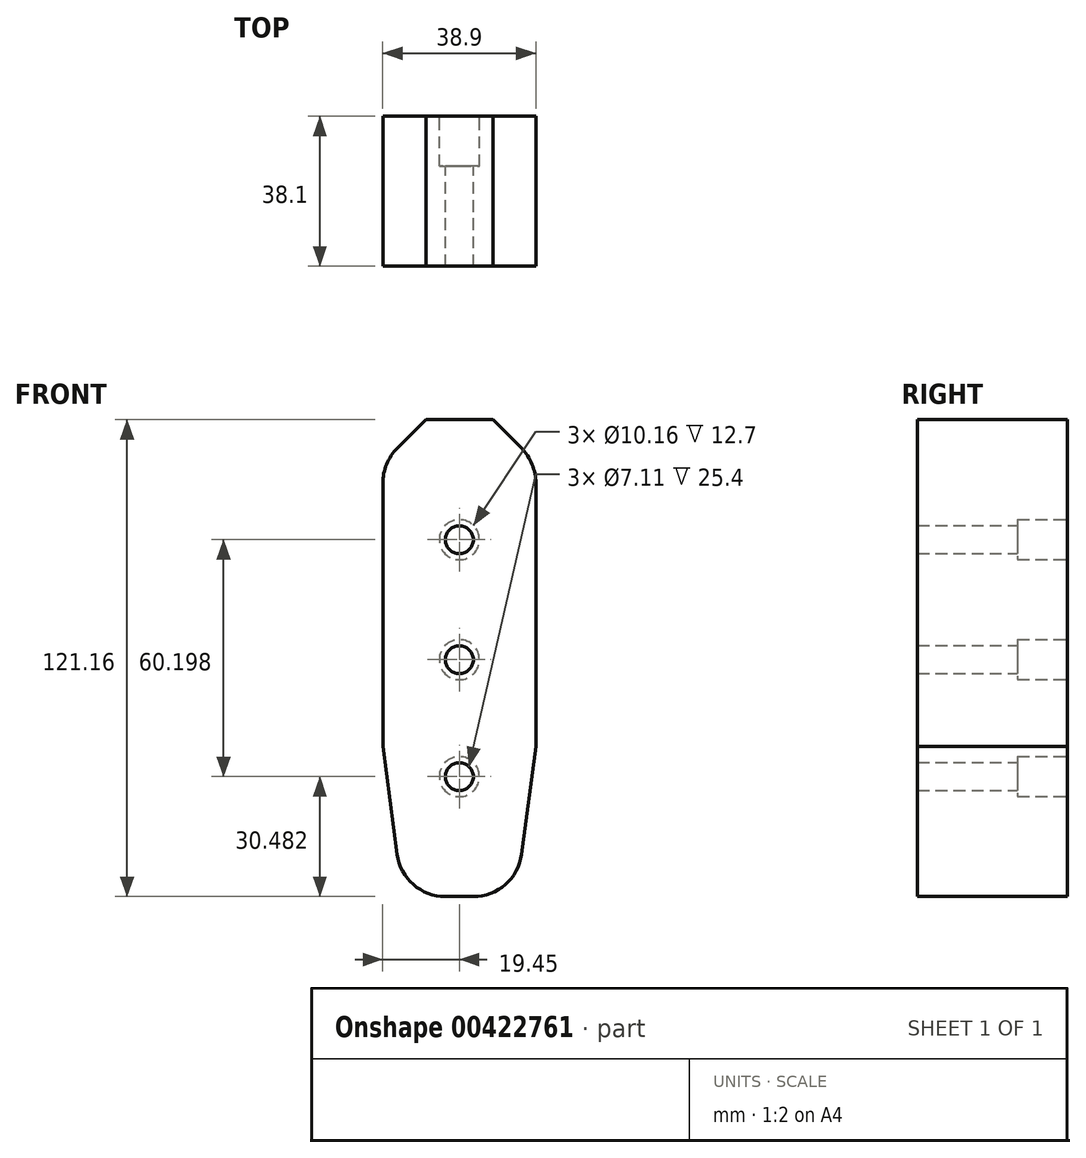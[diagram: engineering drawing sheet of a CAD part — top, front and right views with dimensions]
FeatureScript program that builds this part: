
annotation { "Feature Type Name" : "Feature", "Feature Type Description" : "" }
export const myFeature = defineFeature(function(context is Context, id is Id, definition is map)
    precondition{}
    {
        {
            var Q0;
            Q0=qCreatedBy(makeId("Front.planeOp"),FACE);
            var sketch = newSketch(context, id + "F0", { "sketchPlane" : qUnion([Q0])});
            skLineSegment(sketch, "E0", {"start": v(19.45, 50.8) * mm, "end": v(-19.45, 50.8) * mm});
            skLineSegment(sketch, "E1", {"start": v(19.45, 50.8) * mm, "end": v(19.45, -70.36) * mm});
            skLineSegment(sketch, "E2", {"start": v(-19.45, 50.8) * mm, "end": v(-19.45, -70.36) * mm});
            skLineSegment(sketch, "E3", {"start": v(19.45, -70.36) * mm, "end": v(-19.45, -70.36) * mm});
            skSolve(sketch);
        }
        {
            var Q0;
            Q0 = qSketchRegion(id + "F0", true);
            extrude(context, id + "F1", {"entities" : qUnion([Q0]), "oppositeDirection" : true, "depth" : 38.1 * mm, "offsetDistance" : 25.4 * mm});
        }
        {
            var Q0;
            Q0=makeQuery(id+"F1.opExtrude","SWEPT_EDGE",EDGE,{"disambiguationData":[OSD([sQuery(id+"F0.wireOp",EDGE,"5a9edbc7-dbc8-452a-a94e-e9a3c7398107"),sQuery(id+"F0.wireOp",EDGE,"E0")])]});
            var Q1;
            Q1=makeQuery(id+"F1.opExtrude","SWEPT_EDGE",EDGE,{"disambiguationData":[OSD([sQuery(id+"F0.wireOp",EDGE,"E0"),sQuery(id+"F0.wireOp",EDGE,"e4f6d671-606f-493e-a44e-61b159010204")])]});
            chamfer(context, id + "F2", {"entities" : qUnion([Q0, Q1]), "width" : 10.92 * mm, "tangentPropagation" : true});
        }
        {
            var Q0;
            {var subQ0=sQuery(id+"F0.wireOp",EDGE,"E1");Q0=makeQuery(id+"F2.opChamfer","BLEND_EDGE",EDGE,{"blendedFrom":[makeQuery(id+"F1.opExtrude","SWEPT_EDGE",EDGE,{"disambiguationData":[OSD([sQuery(id+"F0.wireOp",EDGE,"E0"),subQ0])]}),makeQuery(id+"F1.opExtrude","SWEPT_FACE",FACE,{"disambiguationData":[OSD([subQ0])]})],"blendedInto":[makeQuery(id+"F1.opExtrude","SWEPT_FACE",FACE,{"disambiguationData":[OSD([subQ0])]})]});}
            var Q1;
            {var subQ0=sQuery(id+"F0.wireOp",EDGE,"E2");Q1=makeQuery(id+"F2.opChamfer","BLEND_EDGE",EDGE,{"blendedFrom":[makeQuery(id+"F1.opExtrude","SWEPT_EDGE",EDGE,{"disambiguationData":[OSD([sQuery(id+"F0.wireOp",EDGE,"E0"),subQ0])]}),makeQuery(id+"F1.opExtrude","SWEPT_FACE",FACE,{"disambiguationData":[OSD([subQ0])]})],"blendedInto":[makeQuery(id+"F1.opExtrude","SWEPT_FACE",FACE,{"disambiguationData":[OSD([subQ0])]})]});}
            fillet(context, id + "F3", {"entities" : qUnion([Q0, Q1]), "radius" : 12.7 * mm, "tangentPropagation" : true, "allowEdgeOverflow" : false});
        }
        {
            var Q0;
            Q0=makeQuery(id+"F1.opExtrude","SWEPT_EDGE",EDGE,{"disambiguationData":[OSD([sQuery(id+"F0.wireOp",EDGE,"E2"),sQuery(id+"F0.wireOp",EDGE,"E3")])]});
            var Q1;
            Q1=makeQuery(id+"F1.opExtrude","SWEPT_EDGE",EDGE,{"disambiguationData":[OSD([sQuery(id+"F0.wireOp",EDGE,"E1"),sQuery(id+"F0.wireOp",EDGE,"E3")])]});
            chamfer(context, id + "F4", {"entities" : qUnion([Q0, Q1]), "chamferType" : ChamferType.TWO_OFFSETS, "width1" : 38.1 * mm, "oppositeDirection" : false, "width2" : 5.08 * mm, "tangentPropagation" : true});
        }
        {
            var Q0;
            {var subQ0=sQuery(id+"F0.wireOp",EDGE,"E3");Q0=makeQuery(id+"F4.opChamfer","BLEND_EDGE",EDGE,{"blendedFrom":[makeQuery(id+"F1.opExtrude","SWEPT_EDGE",EDGE,{"disambiguationData":[OSD([sQuery(id+"F0.wireOp",EDGE,"E1"),subQ0])]}),makeQuery(id+"F1.opExtrude","SWEPT_FACE",FACE,{"disambiguationData":[OSD([subQ0])]})],"blendedInto":[makeQuery(id+"F1.opExtrude","SWEPT_FACE",FACE,{"disambiguationData":[OSD([subQ0])]})]});}
            var Q1;
            {var subQ0=sQuery(id+"F0.wireOp",EDGE,"E3");Q1=makeQuery(id+"F4.opChamfer","BLEND_EDGE",EDGE,{"blendedFrom":[makeQuery(id+"F1.opExtrude","SWEPT_EDGE",EDGE,{"disambiguationData":[OSD([sQuery(id+"F0.wireOp",EDGE,"E2"),subQ0])]}),makeQuery(id+"F1.opExtrude","SWEPT_FACE",FACE,{"disambiguationData":[OSD([subQ0])]})],"blendedInto":[makeQuery(id+"F1.opExtrude","SWEPT_FACE",FACE,{"disambiguationData":[OSD([subQ0])]})]});}
            fillet(context, id + "F5", {"entities" : qUnion([Q0, Q1]), "radius" : 12.38 * mm, "tangentPropagation" : true, "allowEdgeOverflow" : false});
        }
        {
            var Q0;
            Q0=makeQuery(id+"F1.opExtrude","CAP_FACE",FACE,{"disambiguationData":[OSD([sQuery(id+"F0.wireOp",EDGE,"E0"),sQuery(id+"F0.wireOp",EDGE,"E1"),sQuery(id+"F0.wireOp",EDGE,"E2"),sQuery(id+"F0.wireOp",EDGE,"E3")])],"isStart":false});
            var sketch = newSketch(context, id + "F6", { "sketchPlane" : qUnion([Q0])});
            skCircle(sketch, "E4", {"center": v(0, -39.88) * mm, "radius": 5.08 * mm});
            skCircle(sketch, "E5", {"center": v(0, -10.16) * mm, "radius": 5.08 * mm});
            skCircle(sketch, "E6", {"center": v(0, 20.32) * mm, "radius": 5.08 * mm});
            skCircle(sketch, "E7", {"center": v(0, -10.16) * mm, "radius": 3.56 * mm});
            skCircle(sketch, "E8", {"center": v(0, 20.32) * mm, "radius": 3.56 * mm});
            skCircle(sketch, "E9", {"center": v(0, -39.88) * mm, "radius": 3.56 * mm});
            skSolve(sketch);
        }
        {
            var Q0;
            Q0 = qSketchRegion(id + "F6", true);
            extrude(context, id + "F7", {"entities" : qUnion([Q0]), "operationType" : NewBodyOperationType.REMOVE, "oppositeDirection" : true, "depth" : 12.7 * mm, "offsetDistance" : 25.4 * mm});
        }
        {
            var Q0;
            Q0=makeQuery(id+"F6.imprint","IMPRINT",FACE,{"disambiguationData":[TD([[makeQuery(id+"F6.imprint","IMPRINT",EDGE,{"derivedFrom":sQuery(id+"F6.wireOp",EDGE,"E8")}),1.0]])]});
            var Q1;
            Q1=makeQuery(id+"F6.imprint","IMPRINT",FACE,{"disambiguationData":[TD([[makeQuery(id+"F6.imprint","IMPRINT",EDGE,{"derivedFrom":sQuery(id+"F6.wireOp",EDGE,"E7")}),1.0]])]});
            var Q2;
            Q2=makeQuery(id+"F6.imprint","IMPRINT",FACE,{"disambiguationData":[TD([[makeQuery(id+"F6.imprint","IMPRINT",EDGE,{"derivedFrom":sQuery(id+"F6.wireOp",EDGE,"E9")}),1.0]])]});
            extrude(context, id + "F8", {"entities" : qUnion([Q0, Q1, Q2]), "operationType" : NewBodyOperationType.REMOVE, "endBound" : BoundingType.THROUGH_ALL, "oppositeDirection" : true, "depth" : 25.4 * mm, "offsetDistance" : 25.4 * mm});
        }
    });
